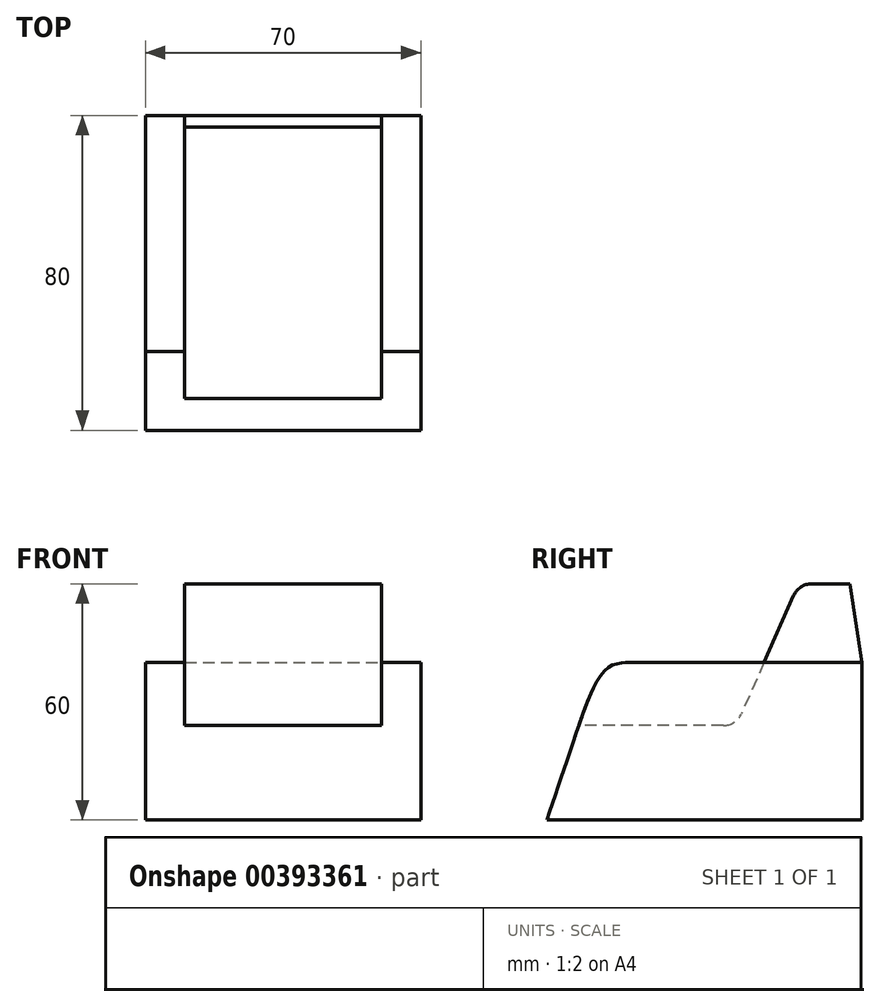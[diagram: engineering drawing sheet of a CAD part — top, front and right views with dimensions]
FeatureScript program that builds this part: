
annotation { "Feature Type Name" : "Feature", "Feature Type Description" : "" }
export const myFeature = defineFeature(function(context is Context, id is Id, definition is map)
    precondition{}
    {
        {
            var Q0;
            Q0=qCreatedBy(makeId("Right.planeOp"),FACE);
            var sketch = newSketch(context, id + "F0", { "sketchPlane" : qUnion([Q0])});
            skLineSegment(sketch, "E0", {"start": v(0, 0) * mm, "end": v(80, 0) * mm});
            skLineSegment(sketch, "E1", {"start": v(80, 0) * mm, "end": v(80, 40) * mm});
            skLineSegment(sketch, "E2", {"start": v(80, 40) * mm, "end": v(20, 40) * mm});
            skFitSpline(sketch, "E3", {"points": [v(0, 0) * mm, v(6.98, 20.68) * mm, v(14.93, 38.21) * mm, v(20, 40) * mm], "startDerivative": vector(16.4, 48.38) * mm, "endDerivative": vector(25.52, 2.11) * mm});
            skSolve(sketch);
        }
        {
            var Q0;
            Q0 = qSketchRegion(id + "F0", true);
            extrude(context, id + "F1", {"entities" : qUnion([Q0]), "depth" : 10 * mm});
        }
        {
            var Q0;
            Q0=makeQuery(id+"F1.opExtrude","CAP_FACE",FACE,{"disambiguationData":[OSD([sQuery(id+"F0.wireOp",EDGE,"E0"),sQuery(id+"F0.wireOp",EDGE,"E1"),sQuery(id+"F0.wireOp",EDGE,"E2"),sQuery(id+"F0.wireOp",EDGE,"E3")])],"isStart":false});
            var sketch = newSketch(context, id + "F2", { "sketchPlane" : qUnion([Q0])});
            skLineSegment(sketch, "E4", {"start": v(80, 0) * mm, "end": v(80, 24) * mm});
            skLineSegment(sketch, "E5", {"start": v(48.1, 24) * mm, "end": v(8.1, 24) * mm});
            skLineSegment(sketch, "E6", {"start": v(8.1, 24) * mm, "end": v(48.1, 24) * mm});
            skLineSegment(sketch, "E7", {"start": v(80, 40) * mm, "end": v(80, 60) * mm});
            skLineSegment(sketch, "E8", {"start": v(80, 60) * mm, "end": v(64, 60) * mm});
            skLineSegment(sketch, "E9", {"start": v(80, 60) * mm, "end": v(74, 60) * mm});
            skLineSegment(sketch, "E10", {"start": v(74, 60) * mm, "end": v(64, 60) * mm});
            skLineSegment(sketch, "E11", {"start": v(64, 60) * mm, "end": v(48.1, 24) * mm});
            skFitSpline(sketch, "E12", {"points": [v(0, 0) * mm, v(6.89, 20.4) * mm, v(8.1, 24) * mm], "startDerivative": vector(11.8, 34.87) * mm, "endDerivative": vector(3.24, 9.71) * mm});
            skLineSegment(sketch, "E13", {"start": v(0, 0) * mm, "end": v(80, 0) * mm});
            skSolve(sketch);
        }
        {
            var Q0;
            Q0 = qSketchRegion(id + "F2", true);
            var Q1;
            {var subQ9=sQuery(id+"F2.wireOp",EDGE,"E4");Q1=makeQuery(id+"F2.imprint","IMPRINT",FACE,{"disambiguationData":[TD([[makeQuery(id+"F2.imprint","IMPRINT",EDGE,{"derivedFrom":subQ9}),1.0]])]});}
            var Q2;
            {var subQ4=sQuery(id+"F2.wireOp",EDGE,"E7");Q2=makeQuery(id+"F2.imprint","IMPRINT",FACE,{"disambiguationData":[TD([[makeQuery(id+"F2.imprint","IMPRINT",EDGE,{"derivedFrom":subQ4}),1.0]])]});}
            extrude(context, id + "F3", {"entities" : qUnion([Q0, Q1, Q2]), "operationType" : NewBodyOperationType.ADD, "depth" : 25 * mm});
        }
        {
            var Q0;
            Q0=makeQuery(id+"F3.opExtrude","SWEPT_EDGE",EDGE,{"disambiguationData":[OSD([sQuery(id+"F0.wireOp",EDGE,"E3"),sQuery(id+"F2.wireOp",EDGE,"E6"),sQuery(id+"F2.wireOp",EDGE,"E12")])]});
            fillet(context, id + "F4", {"entities" : qUnion([Q0]), "radius" : 10 * mm, "tangentPropagation" : true, "allowEdgeOverflow" : false});
        }
        {
            var Q0;
            Q0=makeQuery(id+"F3.opExtrude","SWEPT_EDGE",EDGE,{"disambiguationData":[OSD([sQuery(id+"F2.wireOp",EDGE,"E7"),sQuery(id+"F2.wireOp",EDGE,"E9")])]});
            chamfer(context, id + "F5", {"entities" : qUnion([Q0]), "chamferType" : ChamferType.TWO_OFFSETS, "width1" : 3 * mm, "oppositeDirection" : false, "width2" : 20 * mm, "tangentPropagation" : true});
        }
        {
            var Q0;
            Q0=makeQuery(id+"F3.opExtrude","SWEPT_EDGE",EDGE,{"disambiguationData":[OSD([sQuery(id+"F2.wireOp",EDGE,"E10"),sQuery(id+"F2.wireOp",EDGE,"E11")])]});
            var Q1;
            {var subQ0=sQuery(id+"F2.wireOp",EDGE,"E9");Q1=makeQuery(id+"F5.opChamfer","BLEND_EDGE",EDGE,{"blendedFrom":[makeQuery(id+"F3.opExtrude","SWEPT_EDGE",EDGE,{"disambiguationData":[OSD([sQuery(id+"F2.wireOp",EDGE,"E7"),subQ0])]}),makeQuery(id+"F3.opExtrude","SWEPT_FACE",FACE,{"disambiguationData":[OSD([subQ0,sQuery(id+"F2.wireOp",EDGE,"E10")])]})],"blendedInto":[makeQuery(id+"F3.opExtrude","SWEPT_FACE",FACE,{"disambiguationData":[OSD([subQ0,sQuery(id+"F2.wireOp",EDGE,"E10")])]})]});}
            fillet(context, id + "F6", {"entities" : qUnion([Q0, Q1]), "radius" : 5 * mm, "tangentPropagation" : true, "allowEdgeOverflow" : false});
        }
        {
            var Q0;
            Q0=makeQuery(id+"F1.opExtrude","SWEPT_BODY",BODY,{"disambiguationData":[OSD([sQuery(id+"F0.wireOp",EDGE,"E0"),sQuery(id+"F0.wireOp",EDGE,"E1"),sQuery(id+"F0.wireOp",EDGE,"E2"),sQuery(id+"F0.wireOp",EDGE,"E3")])]});
            var Q1;
            Q1=makeQuery(id+"F3.opExtrude","CAP_FACE",FACE,{"disambiguationData":[OSD([sQuery(id+"F0.wireOp",EDGE,"E1"),sQuery(id+"F0.wireOp",EDGE,"E3"),sQuery(id+"F2.wireOp",EDGE,"E4"),sQuery(id+"F2.wireOp",EDGE,"E6"),sQuery(id+"F2.wireOp",EDGE,"E7"),sQuery(id+"F2.wireOp",EDGE,"E9"),sQuery(id+"F2.wireOp",EDGE,"E10"),sQuery(id+"F2.wireOp",EDGE,"E11"),sQuery(id+"F2.wireOp",EDGE,"E12"),sQuery(id+"F2.wireOp",EDGE,"E13")])],"isStart":false});
            mirror(context, id + "F7", {"operationType" : NewBodyOperationType.ADD, "entities" : qUnion([Q0]), "mirrorPlane" : qUnion([Q1])});
        }
    });
